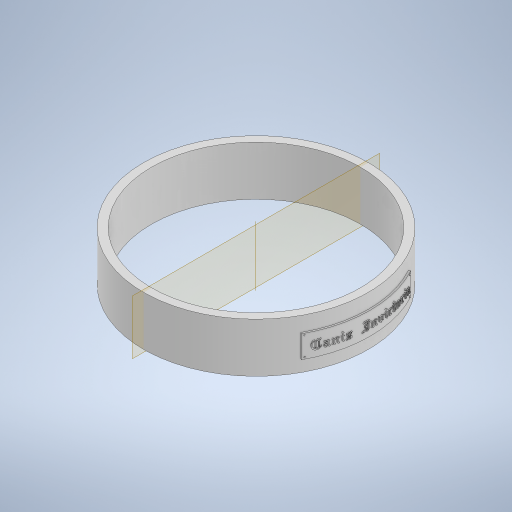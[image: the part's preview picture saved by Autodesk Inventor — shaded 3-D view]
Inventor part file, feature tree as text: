
AUTODESK INVENTOR PART (.ipt)
format: ipt  version: 2023 (Build 270158000, 158)  size: 5,626,368 bytes
history: native  units: in
note: dims shown in document units (in); Inventor stores cm internally (conversion verified against a paired STEP export)
features: emboss x3, pattern_circular x3, other x2, extrude x1, plane x1, fillet x1, sketch x1
ambient origin geometry x8: Origin, YZ Plane, XZ Plane, XY Plane, X Axis, Y Axis, Z Axis, Center Point
bodies: Solid1 (feature_tree)
feature tree (12):
  extrude  "Extrusion1"  Depth=1.9685in
  plane  "Work Plane1"
  other  "Text"
  emboss  "Emboss4"
  emboss  "Emboss5"
  emboss  "Emboss6"
  fillet  "Rivots"  Radius=0.8661in
  pattern_circular  "Circular Pattern1"  Count=6  [1 undecoded]
  pattern_circular  "Circular Pattern2"  [2 undecoded]
  pattern_circular  "Circular Pattern3"  [2 undecoded]
  sketch  "Sketch1"  dims[d0=3.937in d1=3.6614in d2=0.8661in d3=0.0in d4=2.3622in d6=0.4546in d10=0.0in d11=0.3937in d12=1.9685in d19=0.0in d20=0.0in d21=0.0295in d22=0.0in d23=0.0197in d24=0.0in d25=0.0295in d26=0.0295in d27=0.0295in d28=0.0157in d29=0.0in d30=0.0138in d31=0.7874in d32=360.0deg d34=0.7874in d35=360.0deg d37=0.7874in d38=360.0deg d33=0.0in]
  other  "NamePlate"
note: 5 required parameter values undecoded (feature->parameter linkage not recoverable at this tier; creation-order binding heuristic only, values carry confidence <= 0.55)
